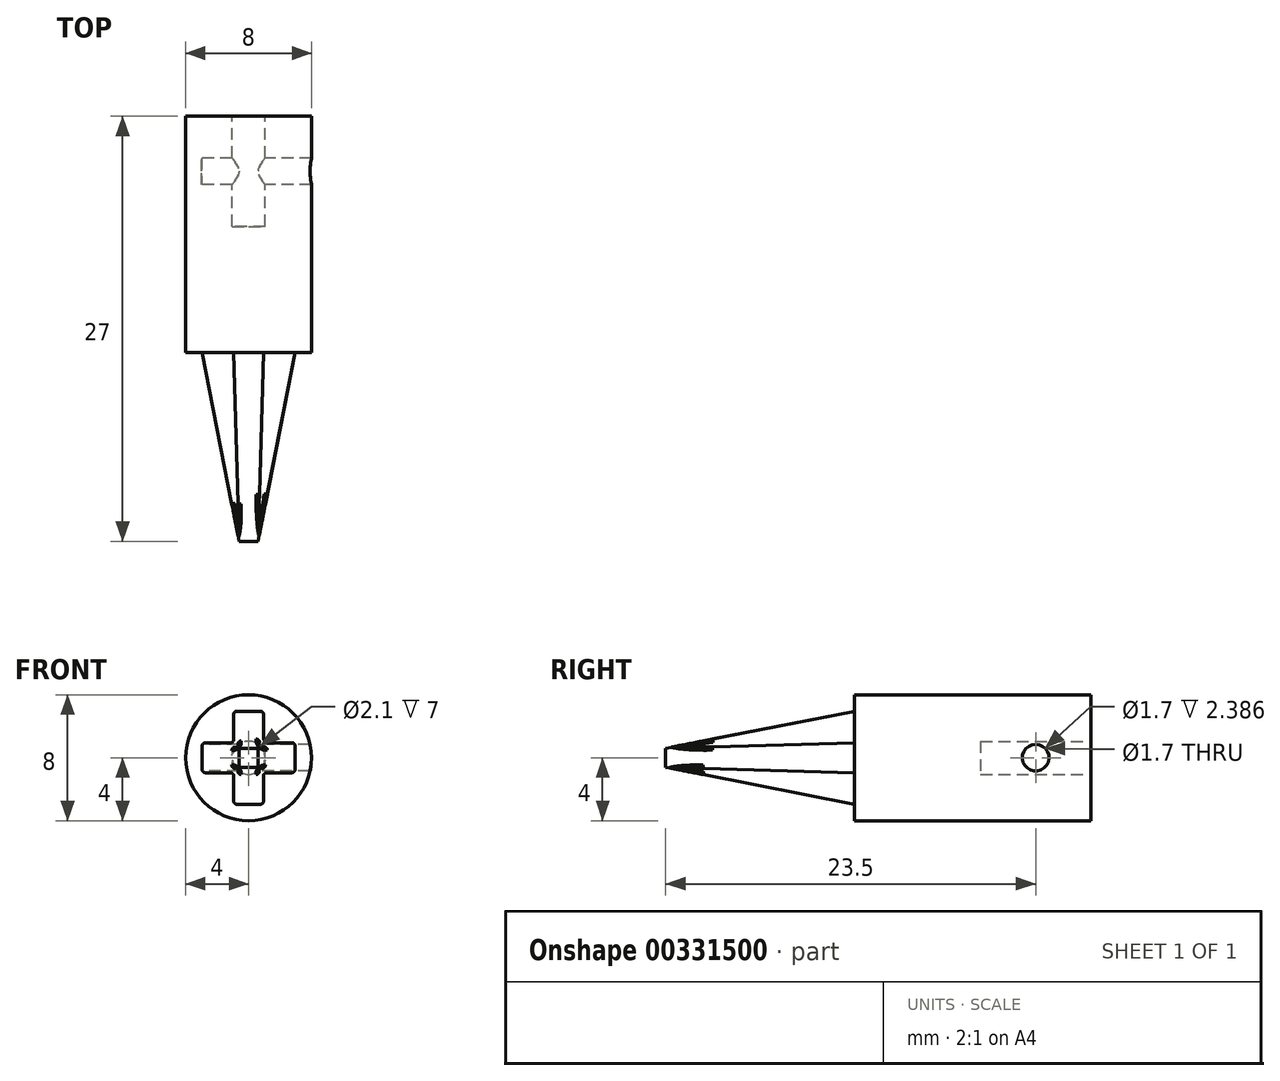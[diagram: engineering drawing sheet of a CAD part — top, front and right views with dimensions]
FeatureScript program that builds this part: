
annotation { "Feature Type Name" : "Feature", "Feature Type Description" : "" }
export const myFeature = defineFeature(function(context is Context, id is Id, definition is map)
    precondition{}
    {
        {
            var Q0;
            Q0=qCreatedBy(makeId("Front.planeOp"),FACE);
            var sketch = newSketch(context, id + "F0", { "sketchPlane" : qUnion([Q0])});
            skCircle(sketch, "E0", {"center": v(3, 3) * mm, "radius": 4 * mm});
            skSolve(sketch);
        }
        {
            var Q0;
            Q0 = qSketchRegion(id + "F0", true);
            extrude(context, id + "F1", {"entities" : qUnion([Q0]), "oppositeDirection" : true, "depth" : 15 * mm});
        }
        {
            var Q0;
            Q0=makeQuery(id+"F1.opExtrude","CAP_FACE",FACE,{"disambiguationData":[OSD([sQuery(id+"F0.wireOp",EDGE,"E0")])],"isStart":false});
            var sketch = newSketch(context, id + "F2", { "sketchPlane" : qUnion([Q0])});
            skCircle(sketch, "E1", {"center": v(-3, 3) * mm, "radius": 1.05 * mm});
            skSolve(sketch);
        }
        {
            var Q0;
            Q0=makeQuery(id+"F2.imprint","IMPRINT",FACE,{"disambiguationData":[TD([[makeQuery(id+"F2.imprint","IMPRINT",EDGE,{"derivedFrom":sQuery(id+"F2.wireOp",EDGE,"E1")}),1.0]])]});
            extrude(context, id + "F3", {"entities" : qUnion([Q0]), "operationType" : NewBodyOperationType.REMOVE, "oppositeDirection" : true, "depth" : 7 * mm});
        }
        {
            var Q0;
            Q0=qCreatedBy(makeId("Right.planeOp"),FACE);
            var sketch = newSketch(context, id + "F4", { "sketchPlane" : qUnion([Q0])});
            skLineSegment(sketch, "E2", {"start": v(0, 0) * mm, "end": v(11.5, 0) * mm});
            skLineSegment(sketch, "E3", {"start": v(11.5, 0) * mm, "end": v(11.5, 3) * mm});
            skSolve(sketch);
        }
        {
            var Q0;
            Q0=sQuery(id+"F4.wireOp",VERTEX,"E3.end");
            var Q1;
            Q1=makeQuery(id+"F1.opExtrude","SWEPT_BODY",BODY,{"disambiguationData":[OSD([sQuery(id+"F0.wireOp",EDGE,"E0")])]});
            hole(context, id + "F5", {"style" : HoleStyle.SIMPLE, "endStyle" : HoleEndStyle.THROUGH, "oppositeDirection" : true, "holeDiameter" : 1.7 * mm, "tappedDepth" : 12 * mm, "tapClearance" : 3, "locations" : qUnion([Q0]), "scope" : qUnion([Q1])});
        }
        {
            var Q0;
            Q0=makeQuery(id+"F1.opExtrude","CAP_FACE",FACE,{"disambiguationData":[OSD([sQuery(id+"F0.wireOp",EDGE,"E0")])],"isStart":true});
            var sketch = newSketch(context, id + "F6", { "sketchPlane" : qUnion([Q0])});
            skLineSegment(sketch, "E4.bottom", {"start": v(2.05, 5.95) * mm, "end": v(3.95, 5.95) * mm});
            skLineSegment(sketch, "E4.top", {"start": v(2.05, 0.05) * mm, "end": v(3.95, 0.05) * mm});
            skLineSegment(sketch, "E4.left", {"start": v(2.05, 5.95) * mm, "end": v(2.05, 0.05) * mm});
            skLineSegment(sketch, "E4.right", {"start": v(3.95, 5.95) * mm, "end": v(3.95, 0.05) * mm});
            skPoint(sketch, "E4.middle", {"position": v(3, 3) * mm});
            skLineSegment(sketch, "E5.bottom", {"start": v(0.05, 3.95) * mm, "end": v(5.95, 3.95) * mm});
            skLineSegment(sketch, "E5.top", {"start": v(0.05, 2.05) * mm, "end": v(5.95, 2.05) * mm});
            skLineSegment(sketch, "E5.left", {"start": v(0.05, 3.95) * mm, "end": v(0.05, 2.05) * mm});
            skLineSegment(sketch, "E5.right", {"start": v(5.95, 3.95) * mm, "end": v(5.95, 2.05) * mm});
            skSolve(sketch);
        }
        {
            var Q0;
            Q0=qCreatedBy(makeId("Front.planeOp"),FACE);
            cPlane(context, id + "F7", {"entities" : qUnion([Q0]), "cplaneType" : CPlaneType.OFFSET, "offset" : 12 * mm, "width" : 150 * mm, "height" : 150 * mm});
        }
        {
            var Q0;
            Q0=qCreatedBy(id+"F7.planeOp",FACE);
            var sketch = newSketch(context, id + "F8", { "sketchPlane" : qUnion([Q0])});
            skLineSegment(sketch, "E6.0.0", {"start": v(2.4, 3.6) * mm, "end": v(2.4, 2.4) * mm});
            skLineSegment(sketch, "E6.0.1", {"start": v(2.4, 2.4) * mm, "end": v(3.6, 2.4) * mm});
            skLineSegment(sketch, "E6.0.2", {"start": v(3.6, 2.4) * mm, "end": v(3.6, 3.6) * mm});
            skLineSegment(sketch, "E6.0.3", {"start": v(3.6, 3.6) * mm, "end": v(2.4, 3.6) * mm});
            skSolve(sketch);
        }
        {
            var Q1;
            Q1=makeQuery(id+"F8.imprint","IMPRINT",FACE,{"disambiguationData":[TD([[makeQuery(id+"F8.imprint","IMPRINT",EDGE,{"derivedFrom":sQuery(id+"F8.wireOp",EDGE,"E6.0.0")}),1.0]])]});
            var Q2;
            {var subQ0=sQuery(id+"F6.wireOp",EDGE,"E5.bottom");var subQ1=sQuery(id+"F6.wireOp",EDGE,"E4.left");var subQ2=makeQuery(id+"F6.imprint","INTERSECT",VERTEX,{"derivedFrom":[subQ1,subQ0]});Q2=makeQuery(id+"F6.imprint","IMPRINT",FACE,{"disambiguationData":[TD([[makeQuery(id+"F6.imprint","IMPRINT",EDGE,{"disambiguationData":[TD([[subQ2,-1.0]])],"derivedFrom":subQ1}),1.0]])]});}
            loft(context, id + "F9", {"operationType" : NewBodyOperationType.ADD, "sheetProfilesArray" : [{ "sheetProfileEntities" : qUnion([Q1]) }, { "sheetProfileEntities" : qUnion([Q2]) }]});
        }
        {
            var Q1;
            Q1=makeQuery(id+"F9.opLoft","CAP_FACE",FACE,{"disambiguationData":[OSD([makeQuery(id+"F8.imprint","IMPRINT",FACE,{"disambiguationData":[TD([[makeQuery(id+"F8.imprint","IMPRINT",EDGE,{"derivedFrom":sQuery(id+"F8.wireOp",EDGE,"E6.0.0")}),1.0]])]})])],"isStart":true});
            var Q2;
            {var subQ5=sQuery(id+"F6.wireOp",EDGE,"E5.right");Q2=makeQuery(id+"F6.imprint","IMPRINT",FACE,{"disambiguationData":[TD([[makeQuery(id+"F6.imprint","IMPRINT",EDGE,{"derivedFrom":subQ5}),-1.0]])]});}
            loft(context, id + "F10", {"operationType" : NewBodyOperationType.ADD, "sheetProfilesArray" : [{ "sheetProfileEntities" : qUnion([Q1]) }, { "sheetProfileEntities" : qUnion([Q2]) }]});
        }
        {
            var Q1;
            {var subQ0=sQuery(id+"F6.wireOp",EDGE,"E4.bottom");Q1=makeQuery(id+"F6.imprint","IMPRINT",FACE,{"disambiguationData":[TD([[makeQuery(id+"F6.imprint","IMPRINT",EDGE,{"derivedFrom":subQ0}),-1.0]])]});}
            var Q2;
            Q2=makeQuery(id+"F9.opLoft","CAP_FACE",FACE,{"disambiguationData":[OSD([makeQuery(id+"F8.imprint","IMPRINT",FACE,{"disambiguationData":[TD([[makeQuery(id+"F8.imprint","IMPRINT",EDGE,{"derivedFrom":sQuery(id+"F8.wireOp",EDGE,"E6.0.0")}),1.0]])]})])],"isStart":true});
            loft(context, id + "F11", {"operationType" : NewBodyOperationType.ADD, "sheetProfilesArray" : [{ "sheetProfileEntities" : qUnion([Q1]) }, { "sheetProfileEntities" : qUnion([Q2]) }]});
        }
        {
            var Q1;
            {var subQ5=sQuery(id+"F6.wireOp",EDGE,"E5.left");Q1=makeQuery(id+"F6.imprint","IMPRINT",FACE,{"disambiguationData":[TD([[makeQuery(id+"F6.imprint","IMPRINT",EDGE,{"derivedFrom":subQ5}),1.0]])]});}
            var Q2;
            Q2=makeQuery(id+"F9.opLoft","CAP_FACE",FACE,{"disambiguationData":[OSD([makeQuery(id+"F8.imprint","IMPRINT",FACE,{"disambiguationData":[TD([[makeQuery(id+"F8.imprint","IMPRINT",EDGE,{"derivedFrom":sQuery(id+"F8.wireOp",EDGE,"E6.0.0")}),1.0]])]})])],"isStart":true});
            loft(context, id + "F12", {"operationType" : NewBodyOperationType.ADD, "sheetProfilesArray" : [{ "sheetProfileEntities" : qUnion([Q1]) }, { "sheetProfileEntities" : qUnion([Q2]) }]});
        }
        {
            var Q1;
            {var subQ0=sQuery(id+"F6.wireOp",EDGE,"E4.top");Q1=makeQuery(id+"F6.imprint","IMPRINT",FACE,{"disambiguationData":[TD([[makeQuery(id+"F6.imprint","IMPRINT",EDGE,{"derivedFrom":subQ0}),1.0]])]});}
            var Q2;
            Q2=makeQuery(id+"F9.opLoft","CAP_FACE",FACE,{"disambiguationData":[OSD([makeQuery(id+"F8.imprint","IMPRINT",FACE,{"disambiguationData":[TD([[makeQuery(id+"F8.imprint","IMPRINT",EDGE,{"derivedFrom":sQuery(id+"F8.wireOp",EDGE,"E6.0.0")}),1.0]])]})])],"isStart":true});
            loft(context, id + "F13", {"operationType" : NewBodyOperationType.ADD, "sheetProfilesArray" : [{ "sheetProfileEntities" : qUnion([Q1]) }, { "sheetProfileEntities" : qUnion([Q2]) }]});
        }
        {
            var Q0;
            {var subQ0=sQuery(id+"F8.wireOp",EDGE,"E6.0.3");var subQ1=sQuery(id+"F8.wireOp",EDGE,"E6.0.2");var subQ2=sQuery(id+"F6.wireOp",EDGE,"E5.bottom");var subQ3=sQuery(id+"F6.wireOp",EDGE,"E4.right");var subQ4=sQuery(id+"F8.wireOp",EDGE,"E6.0.0");Q0=makeQuery(id+"F11.boolean.opBoolean","INTERSECT",EDGE,{"derivedFrom":[makeQuery(id+"F10.boolean.opBoolean","MERGE",FACE,{"derivedFrom":[makeQuery(id+"F9.opLoft","SWEPT_FACE",FACE,{"disambiguationData":[OSD([sQuery(id+"F6.wireOp",EDGE,"E4.left"),subQ3,subQ2,subQ4,subQ1,subQ0])]}),makeQuery(id+"F10.opLoft","SWEPT_FACE",FACE,{"disambiguationData":[OSD([subQ3,subQ2,sQuery(id+"F6.wireOp",EDGE,"E5.right"),subQ4,subQ1,subQ0])]})]}),makeQuery(id+"F11.opLoft","SWEPT_FACE",FACE,{"disambiguationData":[OSD([sQuery(id+"F6.wireOp",EDGE,"E4.bottom"),subQ3,subQ2,sQuery(id+"F8.wireOp",EDGE,"E6.0.1"),subQ1,subQ0])]})]});}
            fillet(context, id + "F14", {"entities" : qUnion([Q0]), "radius" : .3 * mm, "tangentPropagation" : true, "allowEdgeOverflow" : false});
        }
        {
            var Q0;
            {var subQ0=sQuery(id+"F8.wireOp",EDGE,"E6.0.3");var subQ1=sQuery(id+"F8.wireOp",EDGE,"E6.0.0");var subQ2=sQuery(id+"F6.wireOp",EDGE,"E5.bottom");var subQ3=sQuery(id+"F6.wireOp",EDGE,"E4.left");var subQ4=sQuery(id+"F8.wireOp",EDGE,"E6.0.1");Q0=makeQuery(id+"F12.boolean.opBoolean","INTERSECT",EDGE,{"derivedFrom":[makeQuery(id+"F11.boolean.opBoolean","MERGE",FACE,{"derivedFrom":[makeQuery(id+"F9.opLoft","SWEPT_FACE",FACE,{"disambiguationData":[OSD([subQ3,subQ2,sQuery(id+"F6.wireOp",EDGE,"E5.top"),subQ1,subQ4,subQ0])]}),makeQuery(id+"F11.opLoft","SWEPT_FACE",FACE,{"disambiguationData":[OSD([sQuery(id+"F6.wireOp",EDGE,"E4.bottom"),subQ3,subQ2,subQ1,subQ4,subQ0])]})]}),makeQuery(id+"F12.opLoft","SWEPT_FACE",FACE,{"disambiguationData":[OSD([subQ3,subQ2,sQuery(id+"F6.wireOp",EDGE,"E5.left"),subQ1,sQuery(id+"F8.wireOp",EDGE,"E6.0.2"),subQ0])]})]});}
            fillet(context, id + "F15", {"entities" : qUnion([Q0]), "radius" : .2 * mm, "tangentPropagation" : true, "allowEdgeOverflow" : false});
        }
        {
            var Q0;
            {var subQ0=sQuery(id+"F8.wireOp",EDGE,"E6.0.1");var subQ1=sQuery(id+"F8.wireOp",EDGE,"E6.0.0");var subQ2=sQuery(id+"F6.wireOp",EDGE,"E5.top");var subQ3=sQuery(id+"F6.wireOp",EDGE,"E4.left");var subQ4=sQuery(id+"F8.wireOp",EDGE,"E6.0.2");var subQ5=sQuery(id+"F6.wireOp",EDGE,"E4.right");Q0=makeQuery(id+"F13.boolean.opBoolean","INTERSECT",EDGE,{"derivedFrom":[makeQuery(id+"F12.boolean.opBoolean","MERGE",FACE,{"derivedFrom":[makeQuery(id+"F10.boolean.opBoolean","MERGE",FACE,{"derivedFrom":[makeQuery(id+"F9.opLoft","SWEPT_FACE",FACE,{"disambiguationData":[OSD([subQ3,subQ5,subQ2,subQ1,subQ0,subQ4])]}),makeQuery(id+"F10.opLoft","SWEPT_FACE",FACE,{"disambiguationData":[OSD([subQ5,subQ2,sQuery(id+"F6.wireOp",EDGE,"E5.right"),subQ1,subQ0,subQ4])]})]}),makeQuery(id+"F12.opLoft","SWEPT_FACE",FACE,{"disambiguationData":[OSD([subQ3,subQ2,sQuery(id+"F6.wireOp",EDGE,"E5.left"),subQ1,subQ0,subQ4])]})]}),makeQuery(id+"F13.opLoft","SWEPT_FACE",FACE,{"disambiguationData":[OSD([sQuery(id+"F6.wireOp",EDGE,"E4.top"),subQ3,subQ2,subQ1,subQ0,sQuery(id+"F8.wireOp",EDGE,"E6.0.3")])]})]});}
            fillet(context, id + "F16", {"entities" : qUnion([Q0]), "radius" : .2 * mm, "tangentPropagation" : true, "allowEdgeOverflow" : false});
        }
        {
            var Q0;
            {var subQ0=sQuery(id+"F8.wireOp",EDGE,"E6.0.2");var subQ1=sQuery(id+"F8.wireOp",EDGE,"E6.0.1");var subQ2=sQuery(id+"F6.wireOp",EDGE,"E5.top");var subQ3=sQuery(id+"F6.wireOp",EDGE,"E4.right");var subQ4=sQuery(id+"F8.wireOp",EDGE,"E6.0.0");var subQ5=sQuery(id+"F6.wireOp",EDGE,"E4.left");Q0=makeQuery(id+"F13.boolean.opBoolean","INTERSECT",EDGE,{"derivedFrom":[makeQuery(id+"F12.boolean.opBoolean","MERGE",FACE,{"derivedFrom":[makeQuery(id+"F10.boolean.opBoolean","MERGE",FACE,{"derivedFrom":[makeQuery(id+"F9.opLoft","SWEPT_FACE",FACE,{"disambiguationData":[OSD([subQ5,subQ3,subQ2,subQ4,subQ1,subQ0])]}),makeQuery(id+"F10.opLoft","SWEPT_FACE",FACE,{"disambiguationData":[OSD([subQ3,subQ2,sQuery(id+"F6.wireOp",EDGE,"E5.right"),subQ4,subQ1,subQ0])]})]}),makeQuery(id+"F12.opLoft","SWEPT_FACE",FACE,{"disambiguationData":[OSD([subQ5,subQ2,sQuery(id+"F6.wireOp",EDGE,"E5.left"),subQ4,subQ1,subQ0])]})]}),makeQuery(id+"F13.opLoft","SWEPT_FACE",FACE,{"disambiguationData":[OSD([sQuery(id+"F6.wireOp",EDGE,"E4.top"),subQ3,subQ2,subQ1,subQ0,sQuery(id+"F8.wireOp",EDGE,"E6.0.3")])]})]});}
            fillet(context, id + "F17", {"entities" : qUnion([Q0]), "radius" : .2 * mm, "tangentPropagation" : true, "allowEdgeOverflow" : false});
        }
        {
            var Q0;
            Q0=makeQuery(id+"F11.opLoft","SWEPT_EDGE",EDGE,{"disambiguationData":[OSD([sQuery(id+"F6.wireOp",EDGE,"E4.bottom"),sQuery(id+"F6.wireOp",EDGE,"E4.right"),sQuery(id+"F8.wireOp",EDGE,"E6.0.2"),sQuery(id+"F8.wireOp",EDGE,"E6.0.3")])]});
            var Q1;
            Q1=makeQuery(id+"F11.opLoft","SWEPT_EDGE",EDGE,{"disambiguationData":[OSD([sQuery(id+"F6.wireOp",EDGE,"E4.bottom"),sQuery(id+"F6.wireOp",EDGE,"E4.left"),sQuery(id+"F8.wireOp",EDGE,"E6.0.0"),sQuery(id+"F8.wireOp",EDGE,"E6.0.3")])]});
            var Q2;
            Q2=makeQuery(id+"F12.opLoft","SWEPT_EDGE",EDGE,{"disambiguationData":[OSD([sQuery(id+"F6.wireOp",EDGE,"E5.bottom"),sQuery(id+"F6.wireOp",EDGE,"E5.left"),sQuery(id+"F8.wireOp",EDGE,"E6.0.0"),sQuery(id+"F8.wireOp",EDGE,"E6.0.3")])]});
            var Q3;
            Q3=makeQuery(id+"F12.opLoft","SWEPT_EDGE",EDGE,{"disambiguationData":[OSD([sQuery(id+"F6.wireOp",EDGE,"E5.top"),sQuery(id+"F6.wireOp",EDGE,"E5.left"),sQuery(id+"F8.wireOp",EDGE,"E6.0.0"),sQuery(id+"F8.wireOp",EDGE,"E6.0.1")])]});
            var Q4;
            Q4=makeQuery(id+"F13.opLoft","SWEPT_EDGE",EDGE,{"disambiguationData":[OSD([sQuery(id+"F6.wireOp",EDGE,"E4.top"),sQuery(id+"F6.wireOp",EDGE,"E4.left"),sQuery(id+"F8.wireOp",EDGE,"E6.0.0"),sQuery(id+"F8.wireOp",EDGE,"E6.0.1")])]});
            var Q5;
            Q5=makeQuery(id+"F13.opLoft","SWEPT_EDGE",EDGE,{"disambiguationData":[OSD([sQuery(id+"F6.wireOp",EDGE,"E4.top"),sQuery(id+"F6.wireOp",EDGE,"E4.right"),sQuery(id+"F8.wireOp",EDGE,"E6.0.1"),sQuery(id+"F8.wireOp",EDGE,"E6.0.2")])]});
            var Q6;
            Q6=makeQuery(id+"F10.opLoft","SWEPT_EDGE",EDGE,{"disambiguationData":[OSD([sQuery(id+"F6.wireOp",EDGE,"E5.top"),sQuery(id+"F6.wireOp",EDGE,"E5.right"),sQuery(id+"F8.wireOp",EDGE,"E6.0.1"),sQuery(id+"F8.wireOp",EDGE,"E6.0.2")])]});
            var Q7;
            Q7=makeQuery(id+"F10.opLoft","SWEPT_EDGE",EDGE,{"disambiguationData":[OSD([sQuery(id+"F6.wireOp",EDGE,"E5.bottom"),sQuery(id+"F6.wireOp",EDGE,"E5.right"),sQuery(id+"F8.wireOp",EDGE,"E6.0.2"),sQuery(id+"F8.wireOp",EDGE,"E6.0.3")])]});
            fillet(context, id + "F18", {"entities" : qUnion([Q0, Q1, Q2, Q3, Q4, Q5, Q6, Q7]), "radius" : .2 * mm, "tangentPropagation" : true, "allowEdgeOverflow" : false});
        }
    });
